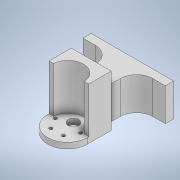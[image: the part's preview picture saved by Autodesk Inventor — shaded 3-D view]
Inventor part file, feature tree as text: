
AUTODESK INVENTOR PART (.ipt)
format: ipt  version: 2020.2 (Build 242310000, 310)  size: 393,216 bytes
history: native  units: mm
features: sketch x12, extrude x9, fillet x5, hole x3
ambient origin geometry x8: Origin, YZ Plane, XZ Plane, XY Plane, X Axis, Y Axis, Z Axis, Center Point
bodies: Solido1 (feature_tree)
feature tree (29):
  extrude  "Estrusione1"  Depth=18.0mm
  extrude  "Estrusione2"  Depth=40.0mm TaperAngle=0.0deg
  extrude  "Estrusione3"  Depth=62.5mm
  extrude  "Estrusione10"  Depth=48.4mm
  hole  "Foro4"  [1 undecoded]
  hole  "Foro5"  [1 undecoded]
  fillet  "Raccordo1"  [1 undecoded]
  fillet  "Raccordo2"  Radius=37.5mm
  fillet  "Raccordo3"  Radius=55.5mm
  extrude  "Estrusione16"  Depth=3.0mm
  hole  "Foro9"  [1 undecoded]
  extrude  "Estrusione17"  Depth=26.0mm
  fillet  "Raccordo5"  Radius=40.0mm
  extrude  "Estrusione19"  Depth=13.0mm
  extrude  "Estrusione20"  TaperAngle=90.0deg  [1 undecoded]
  extrude  "Estrusione21"  Depth=27.0mm
  fillet  "Raccordo6"  [1 undecoded]
  sketch  "Schizzo1"
  sketch  "Schizzo2"
  sketch  "Schizzo3"
  sketch  "Schizzo14"
  sketch  "Schizzo15"
  sketch  "Schizzo16"
  sketch  "Schizzo26"
  sketch  "Schizzo27"
  sketch  "Schizzo28"
  sketch  "Schizzo30"
  sketch  "Schizzo31"
  sketch  "Schizzo32"
note: 6 required parameter values undecoded (feature->parameter linkage not recoverable at this tier; creation-order binding heuristic only, values carry confidence <= 0.55)
